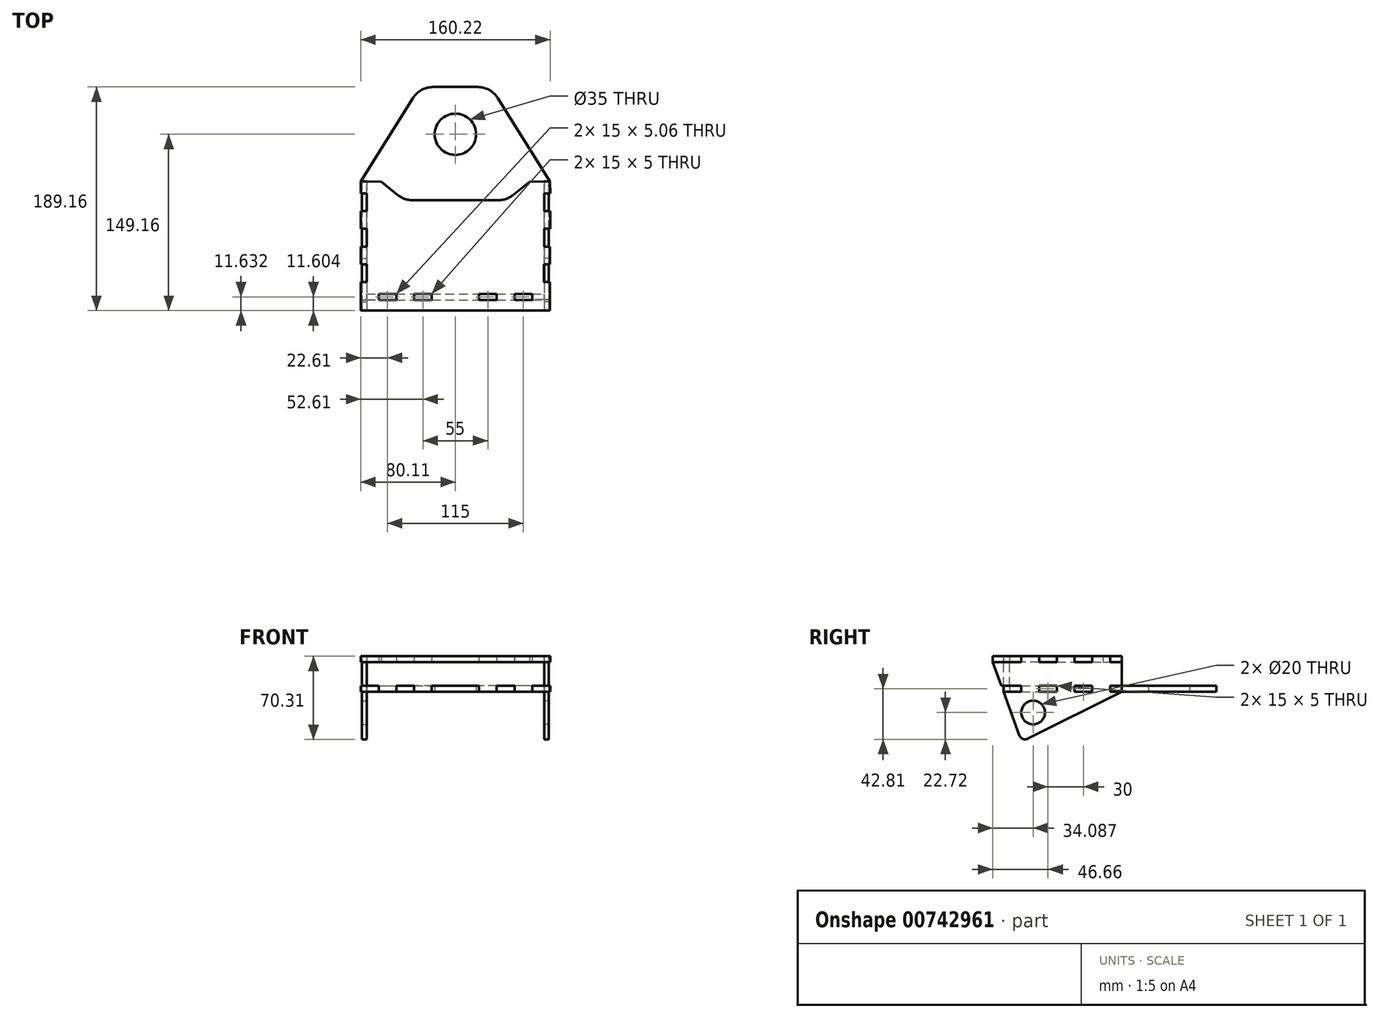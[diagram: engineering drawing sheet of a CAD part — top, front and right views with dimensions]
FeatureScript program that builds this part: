
annotation { "Feature Type Name" : "Feature", "Feature Type Description" : "" }
export const myFeature = defineFeature(function(context is Context, id is Id, definition is map)
    precondition{}
    {
        {
            var Q0;
            Q0=qCreatedBy(makeId("Top.planeOp"),FACE);
            var sketch = newSketch(context, id + "F0", { "sketchPlane" : qUnion([Q0])});
            skLineSegment(sketch, "E0", {"start": v(0, 80) * mm, "end": v(0, 126.1) * mm, "construction": true});
            skLineSegment(sketch, "E1.MirrorCS", {"start": v(-80, 0) * mm, "end": v(-35.88, 70.6) * mm});
            skLineSegment(sketch, "E2.MirrorCS", {"start": v(-18.92, 80) * mm, "end": v(0, 80) * mm});
            skLineSegment(sketch, "E3.MirrorCS", {"start": v(-80, -85) * mm, "end": v(-75, -85) * mm});
            skLineSegment(sketch, "E4.MirrorCS", {"start": v(-80.11, -25) * mm, "end": v(-75.11, -25) * mm});
            skLineSegment(sketch, "E5.MirrorCS", {"start": v(-75.06, -40) * mm, "end": v(-80.11, -40) * mm});
            skLineSegment(sketch, "E6.MirrorCS", {"start": v(-75.11, -10) * mm, "end": v(-80.11, -10) * mm});
            skLineSegment(sketch, "E7.MirrorCS", {"start": v(-80.06, -55) * mm, "end": v(-75.06, -55) * mm});
            skLineSegment(sketch, "E8.MirrorCS", {"start": v(-75, -70) * mm, "end": v(-80.06, -70) * mm});
            skLineSegment(sketch, "E9.MirrorCS", {"start": v(-80, -100) * mm, "end": v(-80, -85) * mm});
            skLineSegment(sketch, "E10.MirrorCS", {"start": v(-75.06, -55) * mm, "end": v(-75.06, -40) * mm});
            skLineSegment(sketch, "E11.MirrorCS", {"start": v(-80.06, -70) * mm, "end": v(-80.06, -55) * mm});
            skLineSegment(sketch, "E12.MirrorCS", {"start": v(-80.11, -10) * mm, "end": v(-80, 0) * mm});
            skLineSegment(sketch, "E13.MirrorCS", {"start": v(-80.11, -40) * mm, "end": v(-80.11, -25) * mm});
            skLineSegment(sketch, "E14.MirrorCS", {"start": v(-75, -85) * mm, "end": v(-75, -70) * mm});
            skLineSegment(sketch, "E15.MirrorCS", {"start": v(-75.11, -25) * mm, "end": v(-75.11, -10) * mm});
            skLineSegment(sketch, "E16.MirrorCS", {"start": v(-20, -95.06) * mm, "end": v(-20, -100.06) * mm});
            skLineSegment(sketch, "E17.MirrorCS", {"start": v(-35, -100.06) * mm, "end": v(-35, -95.06) * mm});
            skLineSegment(sketch, "E18.MirrorCS", {"start": v(-65, -100) * mm, "end": v(-65, -95) * mm});
            skLineSegment(sketch, "E19.MirrorCS", {"start": v(-50, -95) * mm, "end": v(-50, -100.06) * mm});
            skLineSegment(sketch, "E20.MirrorCS", {"start": v(-80, -100) * mm, "end": v(-65, -100) * mm});
            skLineSegment(sketch, "E21.MirrorCS", {"start": v(-35, -95.06) * mm, "end": v(-20, -95.06) * mm});
            skLineSegment(sketch, "E22.MirrorCS", {"start": v(-20, -100.06) * mm, "end": v(0, -100.06) * mm});
            skLineSegment(sketch, "E23.MirrorCS", {"start": v(-50, -100.06) * mm, "end": v(-35, -100.06) * mm});
            skLineSegment(sketch, "E24.MirrorCS", {"start": v(-65, -95) * mm, "end": v(-50, -95) * mm});
            skPoint(sketch, "E25.visualSharp", {"position": v(-30, 80) * mm});
            skArc(sketch, "E26.filletArc", {"start": v(-18.92, 80) * mm, "mid": v(-28.61, 77.5) * mm, "end": v(-35.88, 70.6) * mm});
            skLineSegment(sketch, "E27", {"start": v(0, 0) * mm, "end": v(0, 80) * mm});
            skLineSegment(sketch, "E28.MirrorCS", {"start": v(65, -100) * mm, "end": v(65, -95) * mm});
            skLineSegment(sketch, "E29.MirrorCS", {"start": v(80, -85) * mm, "end": v(75, -85) * mm});
            skLineSegment(sketch, "E30.MirrorCS", {"start": v(80.11, -25) * mm, "end": v(75.11, -25) * mm});
            skLineSegment(sketch, "E31.MirrorCS", {"start": v(75.06, -40) * mm, "end": v(80.11, -40) * mm});
            skLineSegment(sketch, "E32.MirrorCS", {"start": v(75.11, -10) * mm, "end": v(80.11, -10) * mm});
            skLineSegment(sketch, "E33.MirrorCS", {"start": v(35, -100.06) * mm, "end": v(35, -95.06) * mm});
            skLineSegment(sketch, "E34.MirrorCS", {"start": v(20, -95.06) * mm, "end": v(20, -100.06) * mm});
            skLineSegment(sketch, "E35.MirrorCS", {"start": v(50, -95) * mm, "end": v(50, -100.06) * mm});
            skLineSegment(sketch, "E36.MirrorCS", {"start": v(80.11, -10) * mm, "end": v(80, 0) * mm});
            skLineSegment(sketch, "E37.MirrorCS", {"start": v(80.06, -55) * mm, "end": v(75.06, -55) * mm});
            skLineSegment(sketch, "E38.MirrorCS", {"start": v(75, -70) * mm, "end": v(80.06, -70) * mm});
            skLineSegment(sketch, "E39.MirrorCS", {"start": v(75, -85) * mm, "end": v(75, -70) * mm});
            skLineSegment(sketch, "E40.MirrorCS", {"start": v(75.11, -25) * mm, "end": v(75.11, -10) * mm});
            skLineSegment(sketch, "E41.MirrorCS", {"start": v(50, -100.06) * mm, "end": v(35, -100.06) * mm});
            skLineSegment(sketch, "E42.MirrorCS", {"start": v(75.06, -55) * mm, "end": v(75.06, -40) * mm});
            skLineSegment(sketch, "E43.MirrorCS", {"start": v(80.11, -40) * mm, "end": v(80.11, -25) * mm});
            skLineSegment(sketch, "E44.MirrorCS", {"start": v(80.06, -70) * mm, "end": v(80.06, -55) * mm});
            skLineSegment(sketch, "E45.MirrorCS", {"start": v(65, -95) * mm, "end": v(50, -95) * mm});
            skLineSegment(sketch, "E46.MirrorCS", {"start": v(35, -95.06) * mm, "end": v(20, -95.06) * mm});
            skLineSegment(sketch, "E47.MirrorCS", {"start": v(20, -100.06) * mm, "end": v(0, -100.06) * mm});
            skLineSegment(sketch, "E48.MirrorCS", {"start": v(80, -100) * mm, "end": v(65, -100) * mm});
            skLineSegment(sketch, "E49.MirrorCS", {"start": v(80, -100) * mm, "end": v(80, -85) * mm});
            skLineSegment(sketch, "E50.MirrorCS", {"start": v(18.92, 80) * mm, "end": v(0, 80) * mm});
            skArc(sketch, "E51.MirrorCS", {"start": v(18.92, 80) * mm, "mid": v(28.61, 77.5) * mm, "end": v(35.88, 70.6) * mm});
            skLineSegment(sketch, "E52.MirrorCS", {"start": v(80, 0) * mm, "end": v(35.88, 70.6) * mm});
            skCircle(sketch, "E53", {"center": v(0, 40) * mm, "radius": 17.5 * mm});
            skSolve(sketch);
        }
        {
            var Q0;
            Q0 = qSketchRegion(id + "F0", true);
            extrude(context, id + "F1", {"entities" : qUnion([Q0]), "depth" : 5 * mm, "offsetDistance" : 25 * mm});
        }
        {
            var Q0;
            Q0=makeQuery(id+"F1.opExtrude","SWEPT_FACE",FACE,{"disambiguationData":[OSD([sQuery(id+"F0.wireOp",EDGE,"E42.MirrorCS")])]});
            var sketch = newSketch(context, id + "F2", { "sketchPlane" : qUnion([Q0])});
            skLineSegment(sketch, "E54.0", {"start": v(80, 5) * mm, "end": v(70.6, 5) * mm});
            skLineSegment(sketch, "E55.0.1", {"start": v(-40, 0) * mm, "end": v(-40, 5) * mm});
            skLineSegment(sketch, "E55.0.3", {"start": v(-55, 5) * mm, "end": v(-55, 0) * mm});
            skLineSegment(sketch, "E56.0.1", {"start": v(-10, 0) * mm, "end": v(-10, 5) * mm});
            skLineSegment(sketch, "E56.0.3", {"start": v(-25, 5) * mm, "end": v(-25, 0) * mm});
            skLineSegment(sketch, "E57.0.1", {"start": v(-70, 0) * mm, "end": v(-70, 5) * mm});
            skLineSegment(sketch, "E57.0.3", {"start": v(-85, 5) * mm, "end": v(-85, 0) * mm});
            skLineSegment(sketch, "E58.0.1", {"start": v(-85, 0) * mm, "end": v(-85, 5) * mm});
            skLineSegment(sketch, "E59.0.1", {"start": v(-55, 0) * mm, "end": v(-55, 5) * mm});
            skLineSegment(sketch, "E59.0.2", {"start": v(-55, 5) * mm, "end": v(-70, 5) * mm});
            skLineSegment(sketch, "E59.0.3", {"start": v(-70, 5) * mm, "end": v(-70, 0) * mm});
            skLineSegment(sketch, "E60", {"start": v(-100, 15) * mm, "end": v(-60.54, 15) * mm, "construction": true});
            skLineSegment(sketch, "E61", {"start": v(-40, 5) * mm, "end": v(-25, 5) * mm});
            skLineSegment(sketch, "E62.MirrorCS", {"start": v(-85, 25) * mm, "end": v(-85, 30) * mm});
            skLineSegment(sketch, "E63.MirrorCS", {"start": v(-70, 30) * mm, "end": v(-70, 25) * mm});
            skLineSegment(sketch, "E64.MirrorCS", {"start": v(-55, 30) * mm, "end": v(-55, 25) * mm});
            skLineSegment(sketch, "E65.MirrorCS", {"start": v(-70, 25) * mm, "end": v(-70, 30) * mm});
            skLineSegment(sketch, "E66.MirrorCS", {"start": v(-55, 25) * mm, "end": v(-55, 30) * mm});
            skLineSegment(sketch, "E67.MirrorCS", {"start": v(-85, 30) * mm, "end": v(-85, 25) * mm});
            skLineSegment(sketch, "E68.MirrorCS", {"start": v(-40, 30) * mm, "end": v(-40, 25) * mm});
            skLineSegment(sketch, "E69.MirrorCS", {"start": v(-25, 25) * mm, "end": v(-25, 30) * mm});
            skLineSegment(sketch, "E70.MirrorCS", {"start": v(-85, 30) * mm, "end": v(-70, 30) * mm});
            skLineSegment(sketch, "E71.MirrorCS", {"start": v(-10, 30) * mm, "end": v(-10, 25) * mm});
            skLineSegment(sketch, "E72.MirrorCS", {"start": v(-55, 30) * mm, "end": v(-40, 30) * mm});
            skLineSegment(sketch, "E73.MirrorCS", {"start": v(-55, 25) * mm, "end": v(-70, 25) * mm});
            skLineSegment(sketch, "E74.MirrorCS", {"start": v(-85, 25) * mm, "end": v(-100, 25) * mm});
            skLineSegment(sketch, "E75.MirrorCS", {"start": v(-25, 30) * mm, "end": v(-10, 30) * mm});
            skLineSegment(sketch, "E76.MirrorCS", {"start": v(-40, 25) * mm, "end": v(-25, 25) * mm});
            skLineSegment(sketch, "E77.0", {"start": v(-10, 5) * mm, "end": v(0, 5) * mm});
            skLineSegment(sketch, "E78.MirrorCS", {"start": v(-10, 25) * mm, "end": v(0, 25) * mm});
            skLineSegment(sketch, "E79", {"start": v(0, 5) * mm, "end": v(0, 25) * mm});
            skLineSegment(sketch, "E80", {"start": v(-70, 5) * mm, "end": v(-55, 5) * mm});
            skLineSegment(sketch, "E81", {"start": v(0, 0) * mm, "end": v(-79.65, -39.78) * mm});
            skLineSegment(sketch, "E82", {"start": v(-86.58, -37.02) * mm, "end": v(-100.06, 0) * mm});
            skLineSegment(sketch, "E83", {"start": v(0, 0) * mm, "end": v(-10, 0) * mm});
            skLineSegment(sketch, "E84", {"start": v(-100.06, 0) * mm, "end": v(-100.06, -33.72) * mm, "construction": true});
            skCircle(sketch, "E85", {"center": v(-75.07, -17.6) * mm, "radius": 10 * mm});
            skPoint(sketch, "E86.visualSharp", {"position": v(-84.66, -42.29) * mm});
            skArc(sketch, "E86.filletArc", {"start": v(-86.58, -37.02) * mm, "mid": v(-83.74, -39.95) * mm, "end": v(-79.65, -39.78) * mm});
            skLineSegment(sketch, "E87", {"start": v(-100.06, 0) * mm, "end": v(-85, 0) * mm});
            skLineSegment(sketch, "E88", {"start": v(-100.06, 0) * mm, "end": v(-112.28, 33.57) * mm, "construction": true});
            skPoint(sketch, "E58.0.2.end.orphan", {"position": v(-100, 5) * mm});
            skLineSegment(sketch, "E89", {"start": v(-85, 5) * mm, "end": v(-101.88, 5) * mm});
            skLineSegment(sketch, "E90", {"start": v(-101.88, 5) * mm, "end": v(-105.52, 15) * mm});
            skLineSegment(sketch, "E91", {"start": v(-105.52, 15) * mm, "end": v(-109.16, 25) * mm});
            skLineSegment(sketch, "E92", {"start": v(-100, 25) * mm, "end": v(-109.16, 25) * mm});
            skLineSegment(sketch, "E93", {"start": v(-25, 0) * mm, "end": v(-40, 0) * mm});
            skLineSegment(sketch, "E94", {"start": v(-55, 0) * mm, "end": v(-70, 0) * mm});
            skSolve(sketch);
        }
        {
            var Q0;
            Q0 = qSketchRegion(id + "F2", true);
            extrude(context, id + "F3", {"entities" : qUnion([Q0]), "depth" : 4 * mm, "offsetDistance" : 25 * mm});
        }
        {
            var Q0;
            Q0=makeQuery(id+"F3.opExtrude","SWEPT_BODY",BODY,{"disambiguationData":[OSD([sQuery(id+"F2.wireOp",EDGE,"E55.0.1"),sQuery(id+"F2.wireOp",EDGE,"E56.0.0"),sQuery(id+"F2.wireOp",EDGE,"E56.0.1"),sQuery(id+"F2.wireOp",EDGE,"E56.0.3"),sQuery(id+"F2.wireOp",EDGE,"E58.0.1"),sQuery(id+"F2.wireOp",EDGE,"E58.0.2"),sQuery(id+"F2.wireOp",EDGE,"E59.0.1"),sQuery(id+"F2.wireOp",EDGE,"E59.0.2"),sQuery(id+"F2.wireOp",EDGE,"E59.0.3"),sQuery(id+"F2.wireOp",EDGE,"BKiEOMDD-d6MY-yar4-wnMG-8tgpX2SZfHTg"),sQuery(id+"F2.wireOp",EDGE,"qrr8Vlib-MPVu-EEtp-qnUK-Dht6tdSpuVLm"),sQuery(id+"F2.wireOp",EDGE,"pnzOa9am-N8Mo-rOuu-piEG-0ORSU1MNKcDO"),sQuery(id+"F2.wireOp",EDGE,"E61"),sQuery(id+"F2.wireOp",EDGE,"E65.MirrorCS"),sQuery(id+"F2.wireOp",EDGE,"E66.MirrorCS"),sQuery(id+"F2.wireOp",EDGE,"E67.MirrorCS"),sQuery(id+"F2.wireOp",EDGE,"E68.MirrorCS"),sQuery(id+"F2.wireOp",EDGE,"E69.MirrorCS"),sQuery(id+"F2.wireOp",EDGE,"E71.MirrorCS"),sQuery(id+"F2.wireOp",EDGE,"E73.MirrorCS"),sQuery(id+"F2.wireOp",EDGE,"E632.MirrorCS"),sQuery(id+"F2.wireOp",EDGE,"E70.MirrorCS"),sQuery(id+"F2.wireOp",EDGE,"E74.MirrorCS"),sQuery(id+"F2.wireOp",EDGE,"E72.MirrorCS"),sQuery(id+"F2.wireOp",EDGE,"E75.MirrorCS"),sQuery(id+"F2.wireOp",EDGE,"E76.MirrorCS"),sQuery(id+"F2.wireOp",EDGE,"E77.0"),sQuery(id+"F2.wireOp",EDGE,"E78.MirrorCS"),sQuery(id+"F2.wireOp",EDGE,"E79")])]});
            var Q1;
            Q1=qCreatedBy(makeId("Right.planeOp"),FACE);
            mirror(context, id + "F4", {"operationType" : NewBodyOperationType.ADD, "entities" : qUnion([Q0]), "mirrorPlane" : qUnion([Q1])});
        }
        {
            var Q0;
            Q0=makeQuery(id+"F3.opExtrude","SWEPT_FACE",FACE,{"disambiguationData":[OSD([sQuery(id+"F2.wireOp",EDGE,"E73.MirrorCS")])]});
            var sketch = newSketch(context, id + "F5", { "sketchPlane" : qUnion([Q0])});
            skLineSegment(sketch, "E95.0.3", {"start": v(-80, 0) * mm, "end": v(-80.11, -10) * mm});
            skLineSegment(sketch, "E95.0.4", {"start": v(-80.11, -10) * mm, "end": v(-75.11, -10) * mm});
            skLineSegment(sketch, "E95.0.5", {"start": v(-75.11, -10) * mm, "end": v(-75.11, -25) * mm});
            skLineSegment(sketch, "E95.0.6", {"start": v(-75.11, -25) * mm, "end": v(-80.11, -25) * mm});
            skLineSegment(sketch, "E95.0.7", {"start": v(-80.11, -25) * mm, "end": v(-80.11, -40) * mm});
            skLineSegment(sketch, "E95.0.8", {"start": v(-80.11, -40) * mm, "end": v(-75.06, -40) * mm});
            skLineSegment(sketch, "E95.0.9", {"start": v(-75.06, -40) * mm, "end": v(-75.06, -55) * mm});
            skLineSegment(sketch, "E95.0.10", {"start": v(-75.06, -55) * mm, "end": v(-80.06, -55) * mm});
            skLineSegment(sketch, "E95.0.11", {"start": v(-80.06, -55) * mm, "end": v(-80.06, -70) * mm});
            skLineSegment(sketch, "E95.0.12", {"start": v(-80.06, -70) * mm, "end": v(-75, -70) * mm});
            skLineSegment(sketch, "E95.0.13", {"start": v(-75, -70) * mm, "end": v(-75, -85) * mm});
            skLineSegment(sketch, "E95.0.14", {"start": v(-75, -85) * mm, "end": v(-80, -85) * mm});
            skLineSegment(sketch, "E95.0.15", {"start": v(-80, -85) * mm, "end": v(-80, -100) * mm});
            skLineSegment(sketch, "E95.0.17", {"start": v(-65, -100) * mm, "end": v(-65, -95) * mm});
            skLineSegment(sketch, "E95.0.18", {"start": v(-65, -95) * mm, "end": v(-50, -95) * mm});
            skLineSegment(sketch, "E95.0.19", {"start": v(-50, -95) * mm, "end": v(-50, -100.06) * mm});
            skLineSegment(sketch, "E95.0.21", {"start": v(-35, -100.06) * mm, "end": v(-35, -95.06) * mm});
            skLineSegment(sketch, "E95.0.22", {"start": v(-35, -95.06) * mm, "end": v(-20, -95.06) * mm});
            skLineSegment(sketch, "E95.0.23", {"start": v(-20, -95.06) * mm, "end": v(-20, -100.06) * mm});
            skLineSegment(sketch, "E95.0.25", {"start": v(20, -100.06) * mm, "end": v(20, -95.06) * mm});
            skLineSegment(sketch, "E95.0.26", {"start": v(20, -95.06) * mm, "end": v(35, -95.06) * mm});
            skLineSegment(sketch, "E95.0.27", {"start": v(35, -95.06) * mm, "end": v(35, -100.06) * mm});
            skLineSegment(sketch, "E95.0.29", {"start": v(50, -100.06) * mm, "end": v(50, -95) * mm});
            skLineSegment(sketch, "E95.0.30", {"start": v(50, -95) * mm, "end": v(65, -95) * mm});
            skLineSegment(sketch, "E95.0.31", {"start": v(65, -95) * mm, "end": v(65, -100) * mm});
            skLineSegment(sketch, "E95.0.33", {"start": v(80, -100) * mm, "end": v(80, -85) * mm});
            skLineSegment(sketch, "E95.0.34", {"start": v(80, -85) * mm, "end": v(75, -85) * mm});
            skLineSegment(sketch, "E95.0.35", {"start": v(75, -85) * mm, "end": v(75, -70) * mm});
            skLineSegment(sketch, "E95.0.36", {"start": v(75, -70) * mm, "end": v(80.06, -70) * mm});
            skLineSegment(sketch, "E95.0.37", {"start": v(80.06, -70) * mm, "end": v(80.06, -55) * mm});
            skLineSegment(sketch, "E95.0.38", {"start": v(80.06, -55) * mm, "end": v(75.06, -55) * mm});
            skLineSegment(sketch, "E95.0.39", {"start": v(75.06, -55) * mm, "end": v(75.06, -40) * mm});
            skLineSegment(sketch, "E95.0.40", {"start": v(75.06, -40) * mm, "end": v(80.11, -40) * mm});
            skLineSegment(sketch, "E95.0.41", {"start": v(80.11, -40) * mm, "end": v(80.11, -25) * mm});
            skLineSegment(sketch, "E95.0.42", {"start": v(80.11, -25) * mm, "end": v(75.11, -25) * mm});
            skLineSegment(sketch, "E95.0.43", {"start": v(75.11, -25) * mm, "end": v(75.11, -10) * mm});
            skLineSegment(sketch, "E95.0.44", {"start": v(75.11, -10) * mm, "end": v(80.11, -10) * mm});
            skLineSegment(sketch, "E95.0.45", {"start": v(80.11, -10) * mm, "end": v(80, 0) * mm});
            skPoint(sketch, "E96.0.1.end.orphan", {"position": v(-35.88, 70.6) * mm});
            skPoint(sketch, "E96.0.1.start.orphan", {"position": v(-18.92, 80) * mm});
            skLineSegment(sketch, "E97.0", {"start": v(-79.06, -109.16) * mm, "end": v(-75.06, -109.16) * mm});
            skLineSegment(sketch, "E98", {"start": v(-80, -100) * mm, "end": v(-80, -109.16) * mm});
            skLineSegment(sketch, "E99", {"start": v(-80, -109.16) * mm, "end": v(80, -109.16) * mm});
            skLineSegment(sketch, "E100", {"start": v(80, -109.16) * mm, "end": v(80, -100) * mm});
            skPoint(sketch, "E101.0.28.end.orphan", {"position": v(50, -100.06) * mm});
            skLineSegment(sketch, "E102", {"start": v(65, -100) * mm, "end": v(50, -100.06) * mm});
            skLineSegment(sketch, "E103", {"start": v(35, -100.06) * mm, "end": v(20, -100.06) * mm});
            skLineSegment(sketch, "E104", {"start": v(-20, -100.06) * mm, "end": v(-35, -100.06) * mm});
            skLineSegment(sketch, "E105", {"start": v(-50, -100.06) * mm, "end": v(-65, -100) * mm});
            skLineSegment(sketch, "E106", {"start": v(80, 0) * mm, "end": v(62.72, -0.2) * mm});
            skLineSegment(sketch, "E107", {"start": v(62.72, -0.2) * mm, "end": v(48.56, -11.48) * mm});
            skLineSegment(sketch, "E108", {"start": v(36.1, -15.85) * mm, "end": v(0, -15.85) * mm});
            skLineSegment(sketch, "E109", {"start": v(0, -15.85) * mm, "end": v(0, 17.88) * mm, "construction": true});
            skLineSegment(sketch, "E110.MirrorCS", {"start": v(-36.1, -15.85) * mm, "end": v(0, -15.85) * mm});
            skLineSegment(sketch, "E111.MirrorCS", {"start": v(-62.72, -0.2) * mm, "end": v(-48.56, -11.48) * mm});
            skLineSegment(sketch, "E112.MirrorCS", {"start": v(-80, 0) * mm, "end": v(-62.72, -0.2) * mm});
            skPoint(sketch, "E113.visualSharp", {"position": v(-43.09, -15.85) * mm});
            skArc(sketch, "E113.filletArc", {"start": v(-48.56, -11.48) * mm, "mid": v(-42.7, -14.72) * mm, "end": v(-36.1, -15.85) * mm});
            skPoint(sketch, "E114.visualSharp", {"position": v(43.09, -15.85) * mm});
            skArc(sketch, "E114.filletArc", {"start": v(36.1, -15.85) * mm, "mid": v(42.7, -14.72) * mm, "end": v(48.56, -11.48) * mm});
            skSolve(sketch);
        }
        {
            var Q0;
            Q0 = qSketchRegion(id + "F5", true);
            extrude(context, id + "F6", {"entities" : qUnion([Q0]), "depth" : 5 * mm, "offsetDistance" : 25 * mm});
        }
        {
            var Q0;
            Q0=makeQuery(id+"F6.opExtrude","SWEPT_FACE",FACE,{"disambiguationData":[OSD([sQuery(id+"F5.wireOp",EDGE,"E95.0.22")])]});
            var sketch = newSketch(context, id + "F7", { "sketchPlane" : qUnion([Q0])});
            skLineSegment(sketch, "E115.2", {"start": v(-65, 5) * mm, "end": v(-65, 0) * mm});
            skLineSegment(sketch, "E115.3", {"start": v(-35, 5) * mm, "end": v(-35, 0) * mm});
            skLineSegment(sketch, "E115.4", {"start": v(35, 5) * mm, "end": v(35, 0) * mm});
            skLineSegment(sketch, "E115.5", {"start": v(65, 5) * mm, "end": v(65, 0) * mm});
            skFitSpline(sketch, "E115.6", {"points": [v(50, 5) * mm, v(50, 3.33) * mm, v(50, 1.67) * mm, v(50, 0) * mm]});
            skFitSpline(sketch, "E115.7", {"points": [v(-50, 5) * mm, v(-50, 3.33) * mm, v(-50, 1.67) * mm, v(-50, 0) * mm]});
            skLineSegment(sketch, "E115.8", {"start": v(20, 5) * mm, "end": v(20, 0) * mm});
            skLineSegment(sketch, "E115.9", {"start": v(-20, 5) * mm, "end": v(-20, 0) * mm});
            skLineSegment(sketch, "E115.10", {"start": v(65, 30) * mm, "end": v(65, 25) * mm});
            skLineSegment(sketch, "E115.12", {"start": v(-20, 30) * mm, "end": v(-20, 25) * mm});
            skLineSegment(sketch, "E115.14", {"start": v(35, 30) * mm, "end": v(35, 25) * mm});
            skLineSegment(sketch, "E115.15", {"start": v(-65, 30) * mm, "end": v(-65, 25) * mm});
            skLineSegment(sketch, "E115.16", {"start": v(-35, 30) * mm, "end": v(-35, 25) * mm});
            skFitSpline(sketch, "E115.17", {"points": [v(-50, 30) * mm, v(-50, 28.33) * mm, v(-50, 26.67) * mm, v(-50, 25) * mm]});
            skLineSegment(sketch, "E115.18", {"start": v(20, 30) * mm, "end": v(20, 25) * mm});
            skFitSpline(sketch, "E115.19", {"points": [v(50, 30) * mm, v(50, 28.33) * mm, v(50, 26.67) * mm, v(50, 25) * mm]});
            skLineSegment(sketch, "E116", {"start": v(-75.06, 25) * mm, "end": v(-65, 25) * mm});
            skLineSegment(sketch, "E117", {"start": v(-50, 25) * mm, "end": v(-35, 25) * mm});
            skLineSegment(sketch, "E118", {"start": v(-20, 25) * mm, "end": v(20, 25) * mm});
            skLineSegment(sketch, "E119", {"start": v(-20, 30) * mm, "end": v(-35, 30) * mm});
            skLineSegment(sketch, "E120", {"start": v(-50, 30) * mm, "end": v(-65, 30) * mm});
            skLineSegment(sketch, "E121", {"start": v(35, 25) * mm, "end": v(50, 25) * mm});
            skLineSegment(sketch, "E122", {"start": v(65, 25) * mm, "end": v(75.06, 25) * mm});
            skLineSegment(sketch, "E123", {"start": v(65, 30) * mm, "end": v(50, 30) * mm});
            skLineSegment(sketch, "E124", {"start": v(35, 30) * mm, "end": v(20, 30) * mm});
            skLineSegment(sketch, "E125", {"start": v(65, 0) * mm, "end": v(50, 0) * mm});
            skLineSegment(sketch, "E126", {"start": v(35, 0) * mm, "end": v(20, 0) * mm});
            skLineSegment(sketch, "E127", {"start": v(-20, 0) * mm, "end": v(-35, 0) * mm});
            skLineSegment(sketch, "E128", {"start": v(-50, 0) * mm, "end": v(-65, 0) * mm});
            skLineSegment(sketch, "E129", {"start": v(-50, 5) * mm, "end": v(-35, 5) * mm});
            skLineSegment(sketch, "E130", {"start": v(-20, 5) * mm, "end": v(20, 5) * mm});
            skLineSegment(sketch, "E131", {"start": v(35, 5) * mm, "end": v(50, 5) * mm});
            skLineSegment(sketch, "E132", {"start": v(65, 5) * mm, "end": v(75.06, 5) * mm});
            skLineSegment(sketch, "E133", {"start": v(-65, 5) * mm, "end": v(-75.06, 5) * mm});
            skPoint(sketch, "E115.13.start.orphan", {"position": v(80, 30) * mm});
            skPoint(sketch, "E115.1.end.orphan", {"position": v(80, 0) * mm});
            skPoint(sketch, "E115.0.end.orphan", {"position": v(-80, 0) * mm});
            skPoint(sketch, "E115.11.start.orphan", {"position": v(-80, 30) * mm});
            skLineSegment(sketch, "E134.0", {"start": v(75.06, 5) * mm, "end": v(75.06, 25) * mm});
            skLineSegment(sketch, "E135.0", {"start": v(-75.06, 5) * mm, "end": v(-75.06, 25) * mm});
            skPoint(sketch, "E136.orphan", {"position": v(80, 5) * mm});
            skPoint(sketch, "E137.orphan", {"position": v(80, 25) * mm});
            skPoint(sketch, "E138.start.orphan", {"position": v(-80, 5) * mm});
            skPoint(sketch, "E139.orphan", {"position": v(-80, 25) * mm});
            skSolve(sketch);
        }
        {
            var Q0;
            Q0=makeQuery(id+"F7.imprint","IMPRINT",FACE,{"disambiguationData":[TD([[makeQuery(id+"F7.imprint","IMPRINT",EDGE,{"derivedFrom":sQuery(id+"F7.wireOp",EDGE,"E115.2")}),1.0]])]});
            var Q1;
            Q1=makeQuery(id+"F7.imprint","IMPRINT",FACE,{"disambiguationData":[TD([[makeQuery(id+"F7.imprint","IMPRINT",EDGE,{"derivedFrom":sQuery(id+"F7.wireOp",EDGE,"E115.12")}),-1.0]])]});
            extrude(context, id + "F8", {"entities" : qUnion([Q0, Q1]), "depth" : 5 * mm, "offsetDistance" : 25 * mm});
        }
    });
